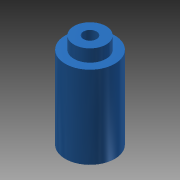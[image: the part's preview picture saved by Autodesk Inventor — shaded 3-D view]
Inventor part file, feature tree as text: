
AUTODESK INVENTOR PART (.ipt)
format: ipt  version: 2013 (Build 170138000, 138)  size: 84,992 bytes
history: native  units: mm
features: extrude x2, sketch x2
ambient origin geometry x8: Origin, YZ Plane, XZ Plane, XY Plane, X Axis, Y Axis, Z Axis, Center Point
bodies: Solid1 (feature_tree)
feature tree (4):
  extrude  "Extrusion1"  Depth=12.0mm
  extrude  "Extrusion2"  Depth=7.8mm
  sketch  "Sketch1"  dims[d0=3.2mm d1=12.0mm]
  sketch  "Sketch2"  dims[d2=20.0mm d3=0.0mm d4=7.8mm d5=3.0mm d6=0.0mm]
